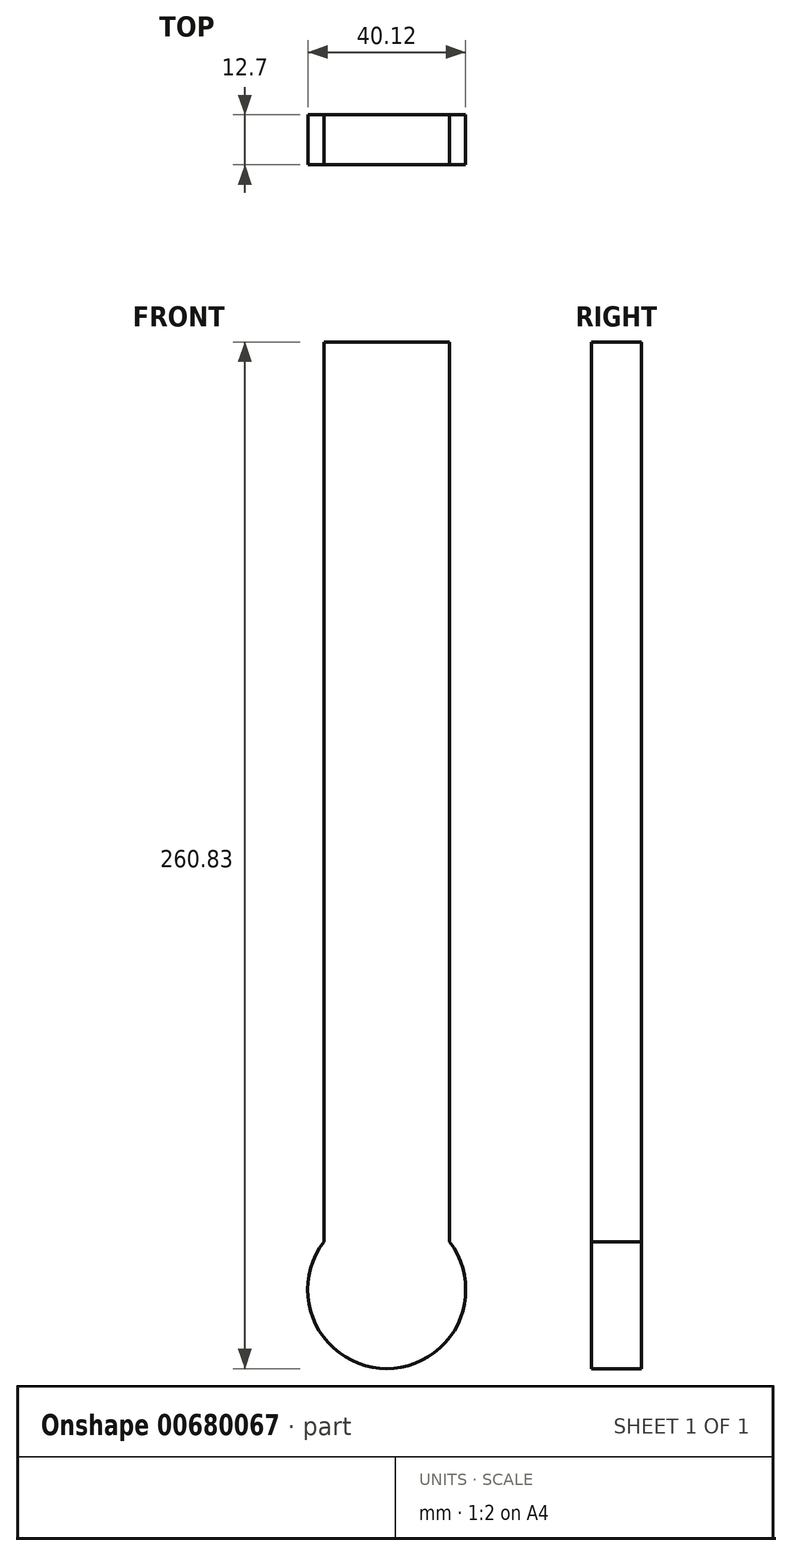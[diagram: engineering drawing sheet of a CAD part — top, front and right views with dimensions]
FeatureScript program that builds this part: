
annotation { "Feature Type Name" : "Feature", "Feature Type Description" : "" }
export const myFeature = defineFeature(function(context is Context, id is Id, definition is map)
    precondition{}
    {
        {
            var Q0;
            Q0=qCreatedBy(makeId("Front.planeOp"),FACE);
            var sketch = newSketch(context, id + "F0", { "sketchPlane" : qUnion([Q0])});
            skCircle(sketch, "E0", {"center": v(0, 0) * mm, "radius": 20.06 * mm});
            skLineSegment(sketch, "E1.bottom", {"start": v(-15.95, 12.17) * mm, "end": v(15.95, 12.17) * mm});
            skLineSegment(sketch, "E1.top", {"start": v(-15.95, 240.77) * mm, "end": v(15.95, 240.77) * mm});
            skLineSegment(sketch, "E1.left", {"start": v(-15.95, 12.17) * mm, "end": v(-15.95, 240.77) * mm});
            skLineSegment(sketch, "E1.right", {"start": v(15.95, 12.17) * mm, "end": v(15.95, 240.77) * mm});
            skSolve(sketch);
        }
        {
            var Q0;
            Q0=makeQuery(id+"F0.imprint","IMPRINT",FACE,{"disambiguationData":[TD([[makeQuery(id+"F0.imprint","IMPRINT",EDGE,{"derivedFrom":sQuery(id+"F0.wireOp",EDGE,"E1.top")}),-1.0]])]});
            var Q1;
            {var subQ0=sQuery(id+"F0.wireOp",EDGE,"E1.bottom");var subQ1=sQuery(id+"F0.wireOp",EDGE,"E0");var subQ3=makeQuery(id+"F0.imprint","INTERSECT",VERTEX,{"derivedFrom":[subQ1,subQ0]});Q1=makeQuery(id+"F0.imprint","IMPRINT",FACE,{"disambiguationData":[TD([[makeQuery(id+"F0.imprint","IMPRINT",EDGE,{"disambiguationData":[TD([[subQ3,1.0]])],"derivedFrom":subQ1}),1.0]])]});}
            var Q2;
            {var subQ0=sQuery(id+"F0.wireOp",EDGE,"E1.bottom");var subQ1=sQuery(id+"F0.wireOp",EDGE,"E0");var subQ3=makeQuery(id+"F0.imprint","INTERSECT",VERTEX,{"derivedFrom":[subQ1,subQ0]});Q2=makeQuery(id+"F0.imprint","IMPRINT",FACE,{"disambiguationData":[TD([[makeQuery(id+"F0.imprint","IMPRINT",EDGE,{"disambiguationData":[TD([[subQ3,-1.0]])],"derivedFrom":subQ1}),1.0]])]});}
            extrude(context, id + "F1", {"entities" : qUnion([Q0, Q1, Q2]), "depth" : 12.7 * mm, "offsetDistance" : 25.4 * mm});
        }
    });
